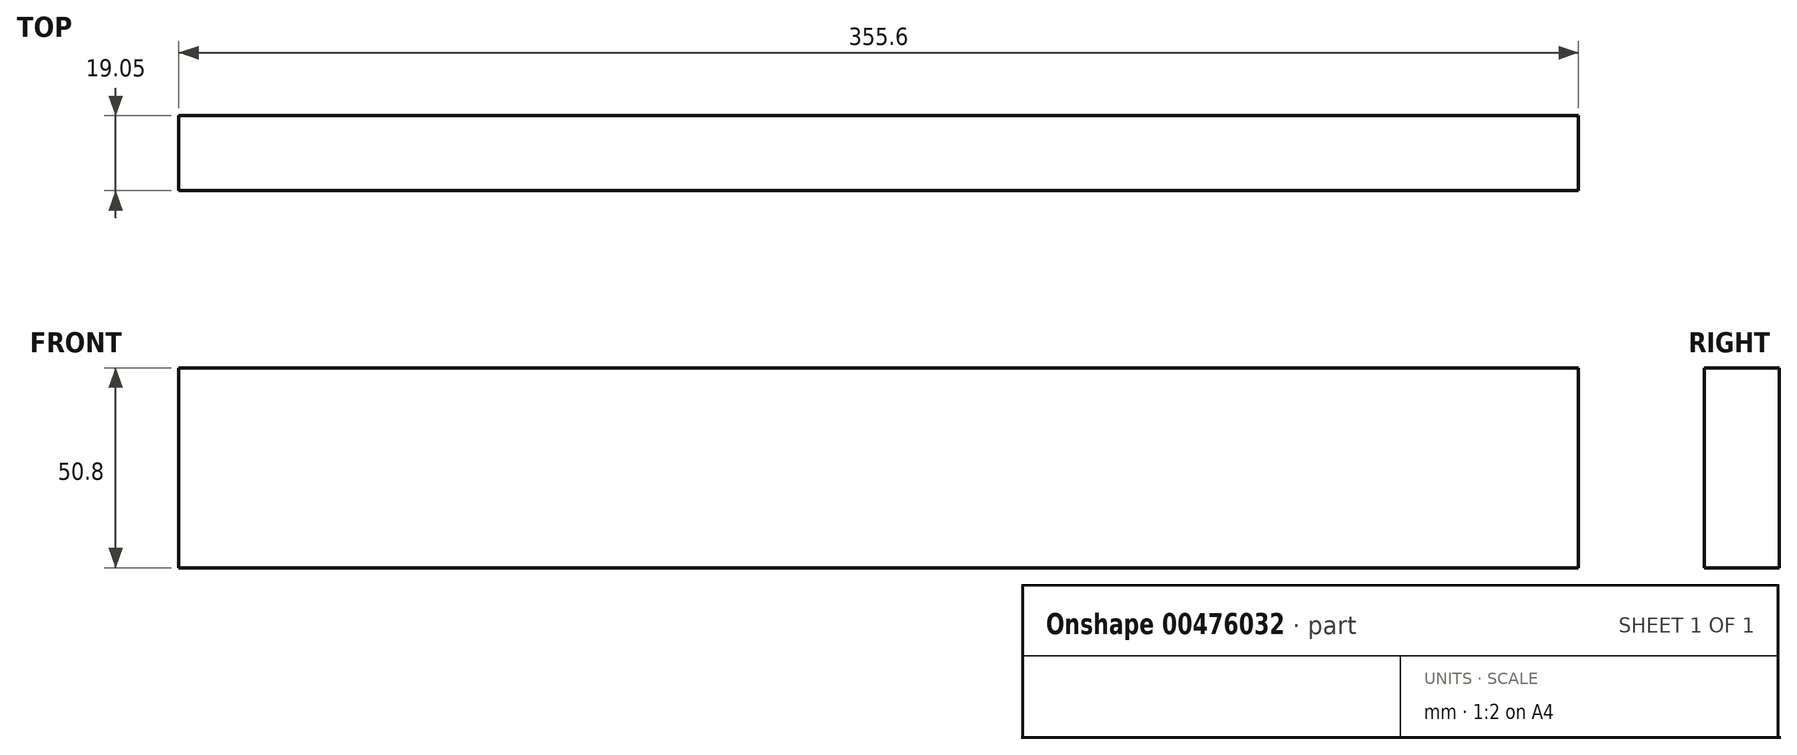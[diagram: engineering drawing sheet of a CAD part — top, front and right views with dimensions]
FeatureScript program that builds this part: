
annotation { "Feature Type Name" : "Feature", "Feature Type Description" : "" }
export const myFeature = defineFeature(function(context is Context, id is Id, definition is map)
    precondition{}
    {
        {
            var Q0;
            Q0=qCreatedBy(makeId("Front.planeOp"),FACE);
            var sketch = newSketch(context, id + "F0", { "sketchPlane" : qUnion([Q0])});
            skLineSegment(sketch, "E0.bottom", {"start": v(0, 0) * mm, "end": v(355.6, 0) * mm});
            skLineSegment(sketch, "E0.top", {"start": v(0, 50.8) * mm, "end": v(355.6, 50.8) * mm});
            skLineSegment(sketch, "E0.left", {"start": v(0, 0) * mm, "end": v(0, 50.8) * mm});
            skLineSegment(sketch, "E0.right", {"start": v(355.6, 0) * mm, "end": v(355.6, 50.8) * mm});
            skSolve(sketch);
        }
        {
            var Q0;
            Q0=makeQuery(id+"F0.imprint","IMPRINT",FACE,{"disambiguationData":[TD([[makeQuery(id+"F0.imprint","IMPRINT",EDGE,{"derivedFrom":sQuery(id+"F0.wireOp",EDGE,"E0.bottom")}),1.0]])]});
            extrude(context, id + "F1", {"entities" : qUnion([Q0]), "depth" : 19.05 * mm});
        }
    });
